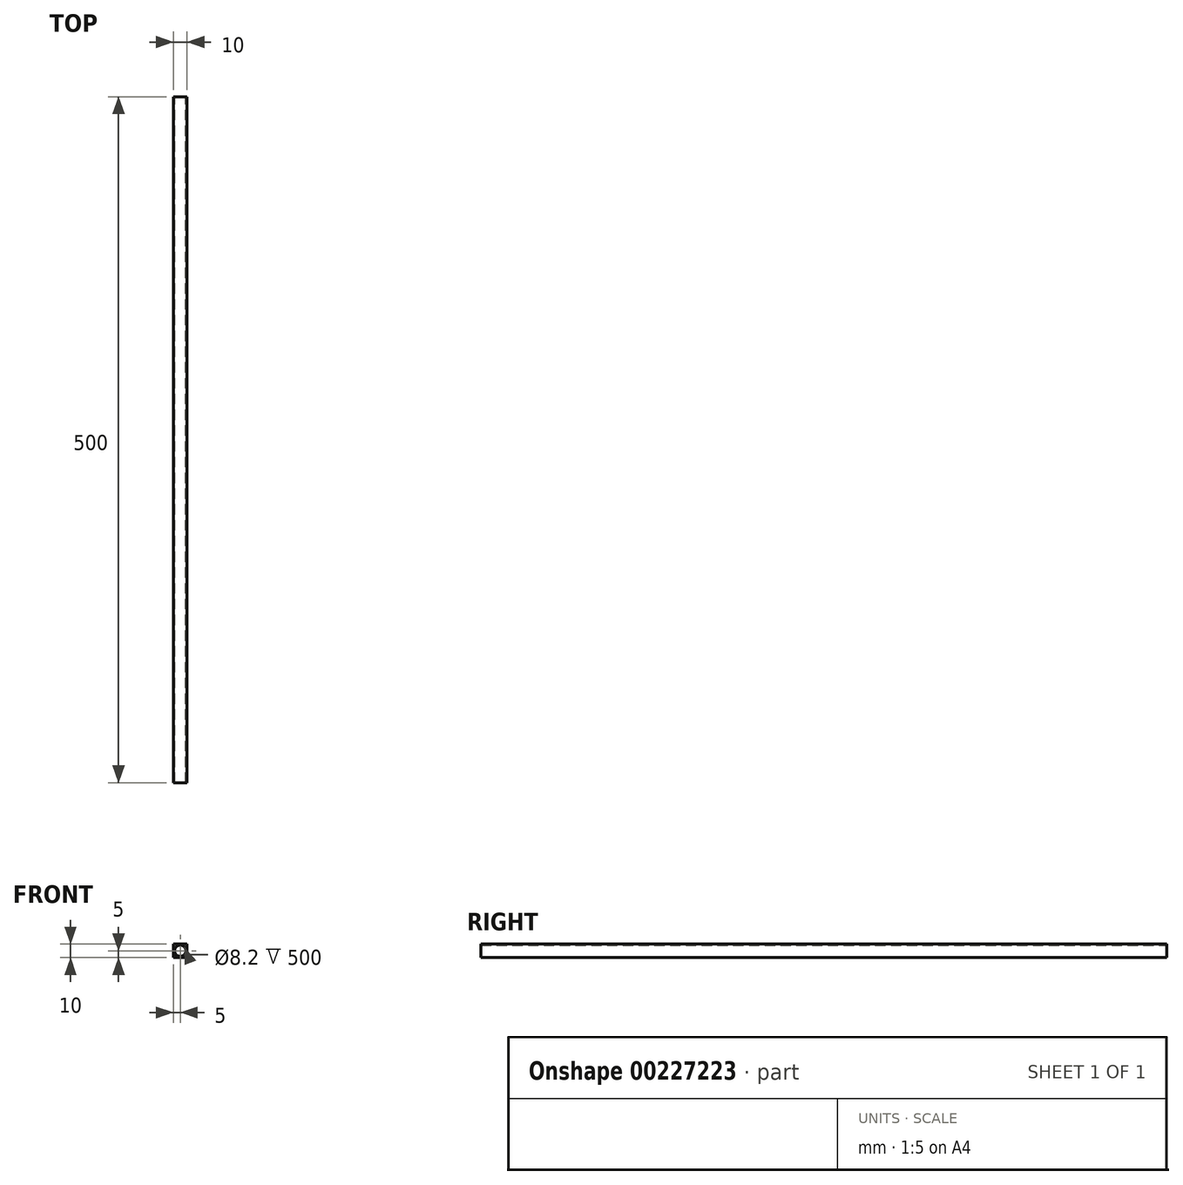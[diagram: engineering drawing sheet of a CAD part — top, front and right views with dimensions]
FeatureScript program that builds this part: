
annotation { "Feature Type Name" : "Feature", "Feature Type Description" : "" }
export const myFeature = defineFeature(function(context is Context, id is Id, definition is map)
    precondition{}
    {
        {
            var Q0;
            Q0=qCreatedBy(makeId("Front.planeOp"),FACE);
            var sketch = newSketch(context, id + "F0", { "sketchPlane" : qUnion([Q0])});
            skLineSegment(sketch, "E0.bottom", {"start": v(5, -5) * mm, "end": v(-5, -5) * mm});
            skLineSegment(sketch, "E0.top", {"start": v(5, 5) * mm, "end": v(-5, 5) * mm});
            skLineSegment(sketch, "E0.left", {"start": v(5, -5) * mm, "end": v(5, 5) * mm});
            skLineSegment(sketch, "E0.right", {"start": v(-5, -5) * mm, "end": v(-5, 5) * mm});
            skPoint(sketch, "E0.middle", {"position": v(0, 0) * mm});
            skCircle(sketch, "E1", {"center": v(0, 0) * mm, "radius": 4.1 * mm});
            skSolve(sketch);
        }
        {
            var Q0;
            Q0 = qSketchRegion(id + "F0", true);
            extrude(context, id + "F1", {"entities" : qUnion([Q0]), "depth" : 500 * mm});
        }
    });
